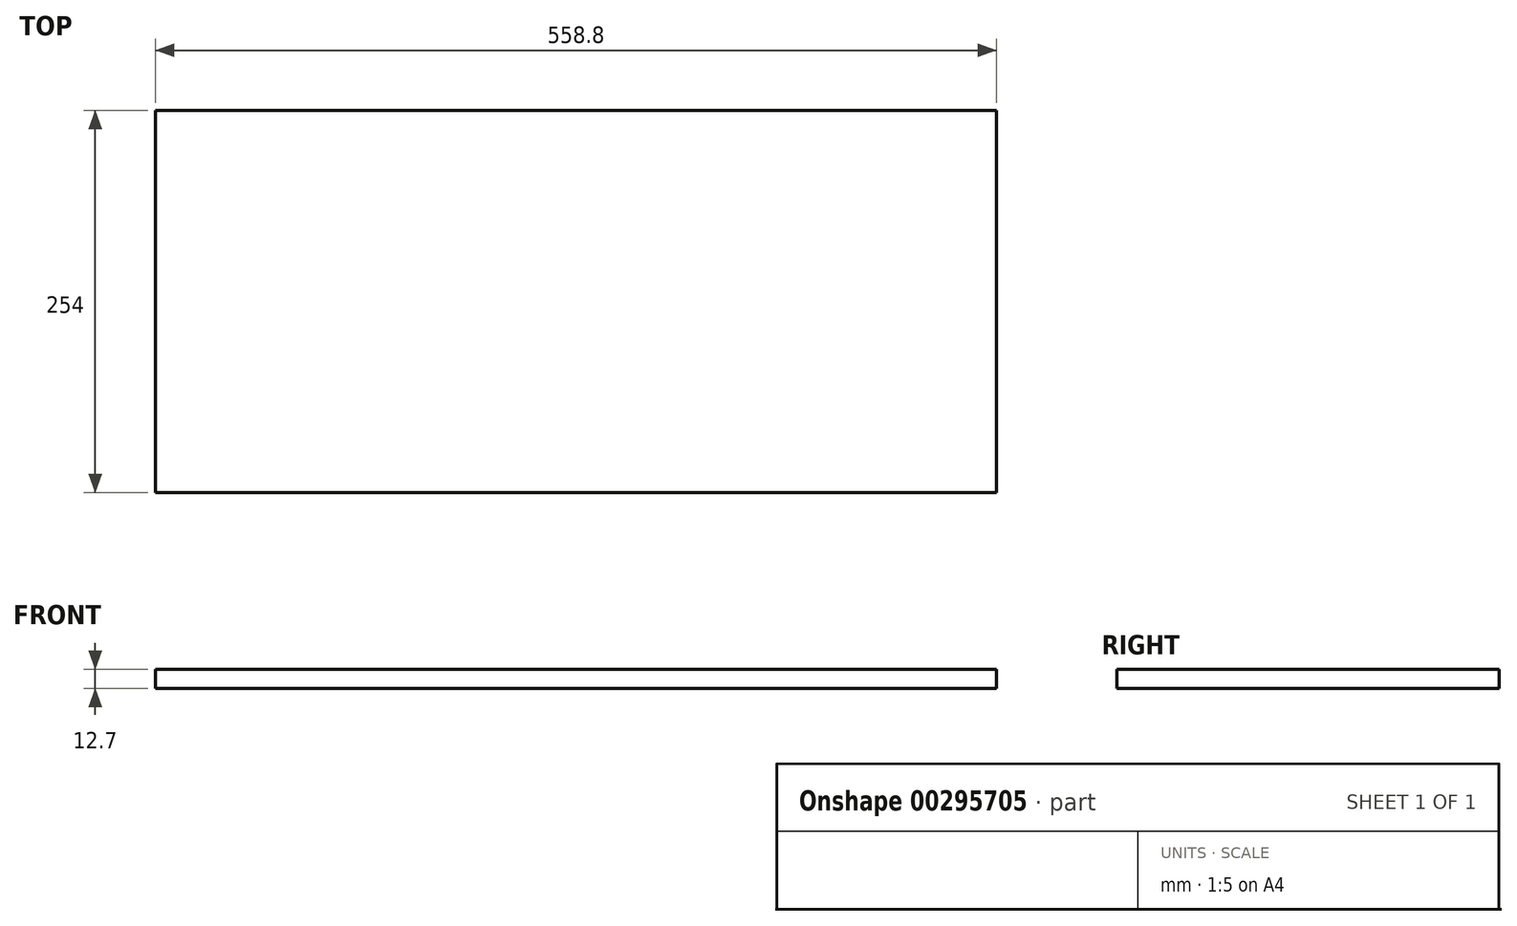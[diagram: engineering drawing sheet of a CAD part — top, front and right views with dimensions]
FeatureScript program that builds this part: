
annotation { "Feature Type Name" : "Feature", "Feature Type Description" : "" }
export const myFeature = defineFeature(function(context is Context, id is Id, definition is map)
    precondition{}
    {
        {
            var Q0;
            Q0=qCreatedBy(makeId("Top.planeOp"),FACE);
            var sketch = newSketch(context, id + "F0", { "sketchPlane" : qUnion([Q0])});
            skLineSegment(sketch, "E0.bottom", {"start": v(279.4, 127) * mm, "end": v(-279.4, 127) * mm});
            skLineSegment(sketch, "E0.top", {"start": v(279.4, -127) * mm, "end": v(-279.4, -127) * mm});
            skLineSegment(sketch, "E0.left", {"start": v(279.4, 127) * mm, "end": v(279.4, -127) * mm});
            skLineSegment(sketch, "E0.right", {"start": v(-279.4, 127) * mm, "end": v(-279.4, -127) * mm});
            skPoint(sketch, "E0.middle", {"position": v(0, 0) * mm});
            skSolve(sketch);
        }
        {
            var Q0;
            Q0 = qSketchRegion(id + "F0", true);
            extrude(context, id + "F1", {"entities" : qUnion([Q0]), "endBound" : BoundingType.SYMMETRIC, "depth" : 12.7 * mm});
        }
    });
